# Revit family: ARKOSLIGHT_Fancy Shape Base 3
name_source: partatom
category: Lighting Fixtures
units: mm (PartAtom-declared; Revit-internal decimal feet)

## family parameters
Cut with Voids When Loaded = No
Host = Face
Light Source = No
Part Type = Normal
Room Calculation Point = No
Round Connector Dimension = Use Diameter
Shared = No

## types (4) — shared parameters
ARKOSLIGHT_Apparent Load = 28 VA
ARKOSLIGHT_Body_Secundary_Color = ARKOSLIGHT_Textured black
ARKOSLIGHT_Fixture Type = ACCESSORIES
ARKOSLIGHT_IP = 20
ARKOSLIGHT_Model = FANCY SHAPE BASE
ARKOSLIGHT_Series = FANCY SHAPE BASE 3
Apparent Load = 28 VA
Manufacturer = ARKOSLIGHT
Model = FANCY SHAPE BASE
URL = https://www.arkoslight.com
zero-valued in all types: Default Elevation

## per-type parameters (varying)
| type | ARKOSLIGHT_Body_Color | ARKOSLIGHT_Color | ARKOSLIGHT_Dimming | ARKOSLIGHT_Reference | ARKOSLIGHT_Wattage |
| A4170221NT - FANCY SHAPE BASE 3 550mA NT | ARKOSLIGHT_Textured black | Textured black | No Dim | A4170221NT | 33 W |
| A4170221WT - FANCY SHAPE BASE 3 550mA WT | ARKOSLIGHT_Textured white | Textured white | No Dim | A4170221WT | 33 W |
| A4170222NT - FANCY SHAPE BASE 3 550mA DIM DALI NT | ARKOSLIGHT_Textured black | Textured black | DALI | A4170222NT | 32 W |
| A4170222WT - FANCY SHAPE BASE 3 550mA DIM DALI WT | ARKOSLIGHT_Textured white | Textured white | DALI | A4170222WT | 32 W |

## geometry (parser evidence)
native form markers: Sweep x2
no freeform markers — native parametric forms only
